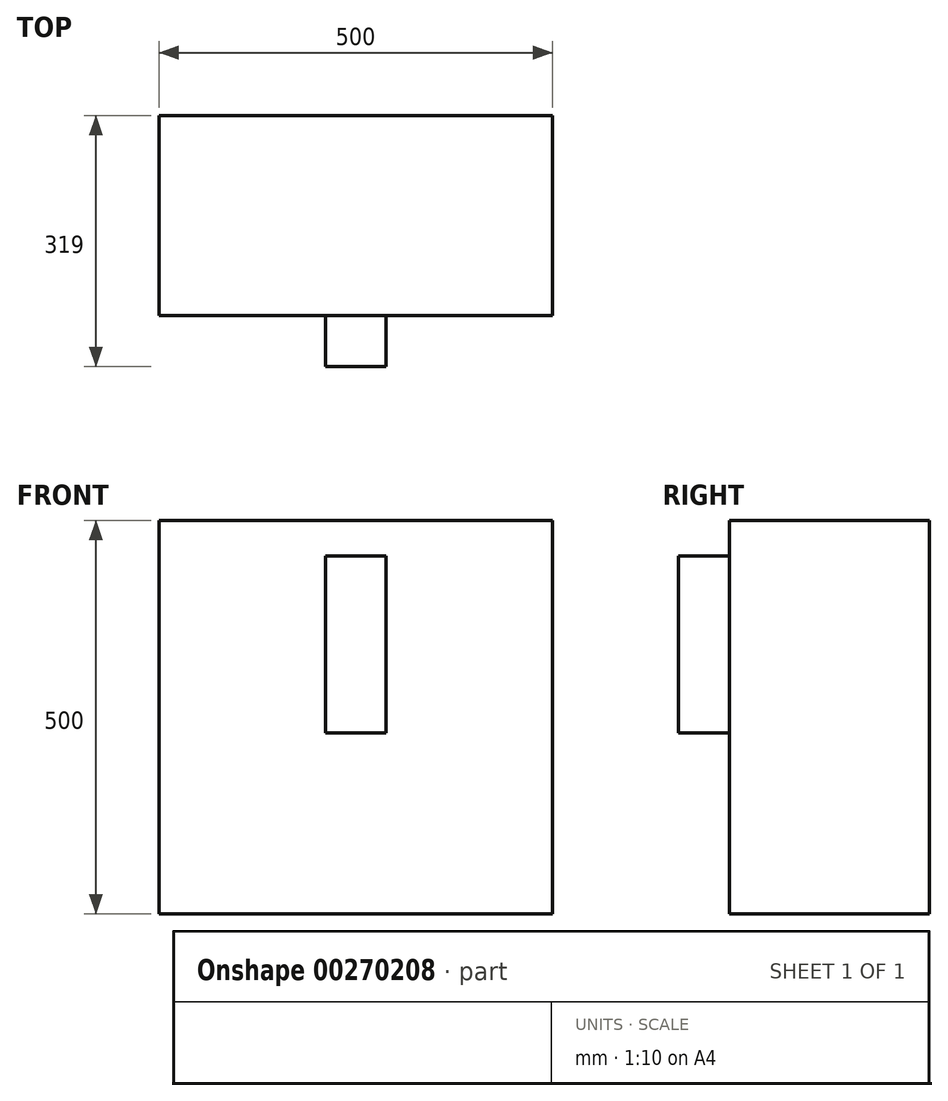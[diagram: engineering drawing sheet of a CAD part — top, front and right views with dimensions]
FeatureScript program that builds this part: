
annotation { "Feature Type Name" : "Feature", "Feature Type Description" : "" }
export const myFeature = defineFeature(function(context is Context, id is Id, definition is map)
    precondition{}
    {
        {
            var Q0;
            Q0=qCreatedBy(makeId("Front.planeOp"),FACE);
            var sketch = newSketch(context, id + "F0", { "sketchPlane" : qUnion([Q0])});
            skLineSegment(sketch, "E0.bottom", {"start": v(250, -250) * mm, "end": v(-250, -250) * mm});
            skLineSegment(sketch, "E0.top", {"start": v(250, 250) * mm, "end": v(-250, 250) * mm});
            skLineSegment(sketch, "E0.left", {"start": v(250, -250) * mm, "end": v(250, 250) * mm});
            skLineSegment(sketch, "E0.right", {"start": v(-250, -250) * mm, "end": v(-250, 250) * mm});
            skPoint(sketch, "E0.middle", {"position": v(0, 0) * mm});
            skSolve(sketch);
        }
        {
            var Q0;
            Q0=makeQuery(id+"F0.imprint","IMPRINT",FACE,{"disambiguationData":[TD([[makeQuery(id+"F0.imprint","IMPRINT",EDGE,{"derivedFrom":sQuery(id+"F0.wireOp",EDGE,"E0.bottom")}),-1.0]])]});
            extrude(context, id + "F1", {"entities" : qUnion([Q0]), "depth" : 254 * mm});
        }
        {
            var Q0;
            Q0=makeQuery(id+"F1.opExtrude","CAP_FACE",FACE,{"disambiguationData":[OSD([sQuery(id+"F0.wireOp",EDGE,"E0.bottom"),sQuery(id+"F0.wireOp",EDGE,"E0.top"),sQuery(id+"F0.wireOp",EDGE,"E0.left"),sQuery(id+"F0.wireOp",EDGE,"E0.right")])],"isStart":false});
            var sketch = newSketch(context, id + "F2", { "sketchPlane" : qUnion([Q0])});
            skLineSegment(sketch, "E1.bottom", {"start": v(38.35, -20.43) * mm, "end": v(-38.35, -20.43) * mm});
            skLineSegment(sketch, "E1.top", {"start": v(38.35, 204.66) * mm, "end": v(-38.35, 204.66) * mm});
            skLineSegment(sketch, "E1.left", {"start": v(38.35, -20.43) * mm, "end": v(38.35, 204.66) * mm});
            skLineSegment(sketch, "E1.right", {"start": v(-38.35, -20.43) * mm, "end": v(-38.35, 204.66) * mm});
            skPoint(sketch, "E1.middle", {"position": v(0, 92.11) * mm});
            skSolve(sketch);
        }
        {
            var Q0;
            Q0=makeQuery(id+"F2.imprint","IMPRINT",FACE,{"disambiguationData":[TD([[makeQuery(id+"F2.imprint","IMPRINT",EDGE,{"derivedFrom":sQuery(id+"F2.wireOp",EDGE,"E1.bottom")}),-1.0]])]});
            extrude(context, id + "F3", {"entities" : qUnion([Q0]), "operationType" : NewBodyOperationType.ADD, "depth" : 65 * mm});
        }
    });
